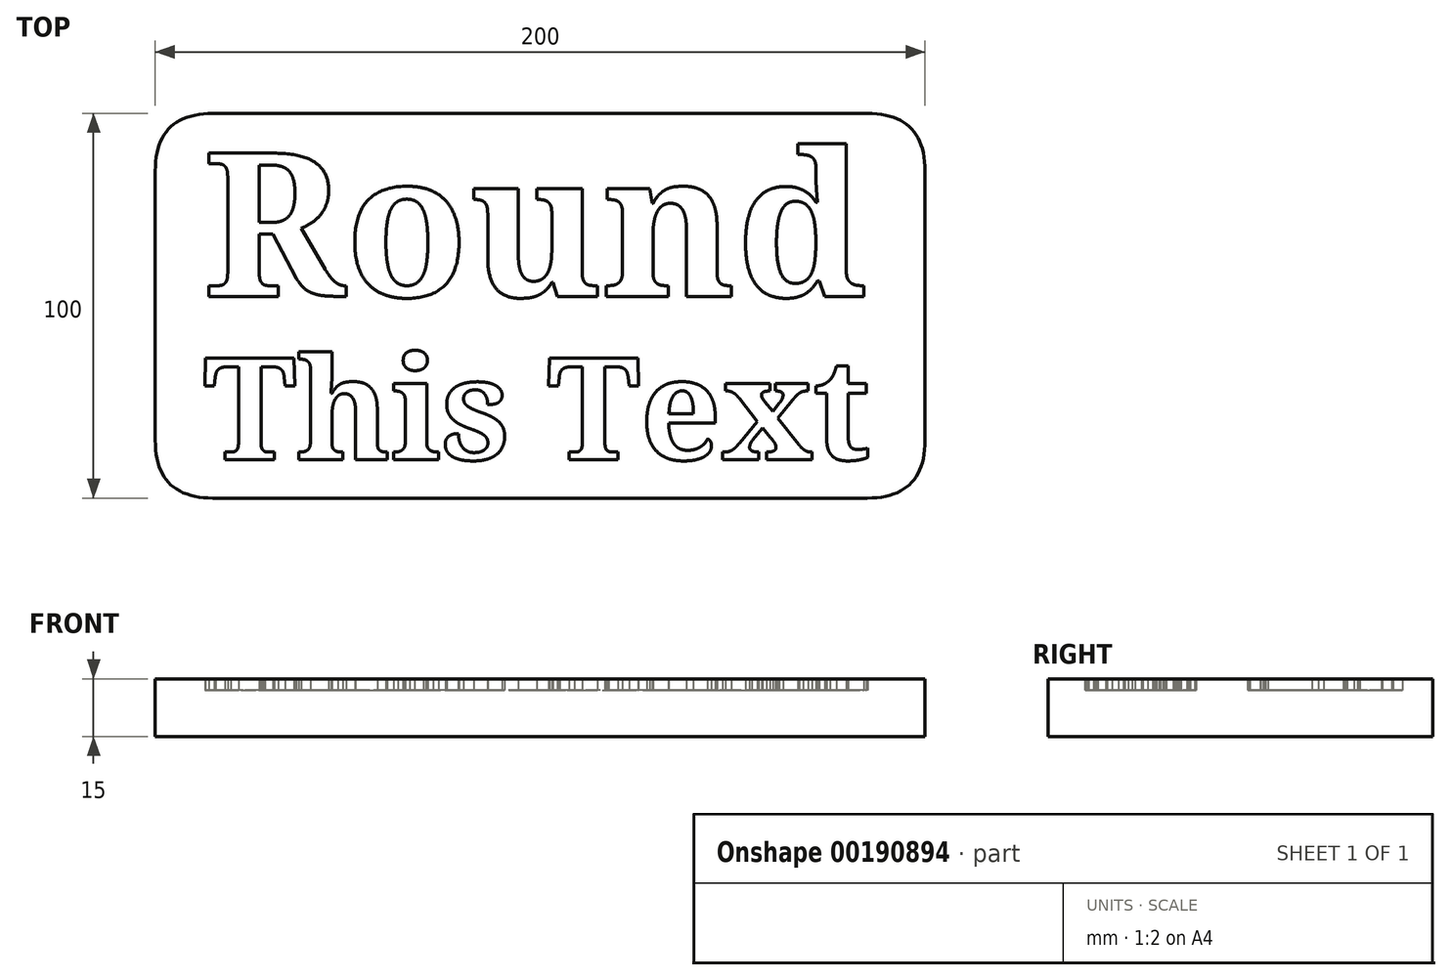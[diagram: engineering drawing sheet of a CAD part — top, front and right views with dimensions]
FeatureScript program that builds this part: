
annotation { "Feature Type Name" : "Feature", "Feature Type Description" : "" }
export const myFeature = defineFeature(function(context is Context, id is Id, definition is map)
    precondition{}
    {
        {
            var Q0;
            Q0=qCreatedBy(makeId("Top.planeOp"),FACE);
            var sketch = newSketch(context, id + "F0", { "sketchPlane" : qUnion([Q0])});
            skLineSegment(sketch, "E0.bottom", {"start": v(100, 50) * mm, "end": v(-100, 50) * mm});
            skLineSegment(sketch, "E0.top", {"start": v(100, -50) * mm, "end": v(-100, -50) * mm});
            skLineSegment(sketch, "E0.left", {"start": v(100, 50) * mm, "end": v(100, -50) * mm});
            skLineSegment(sketch, "E0.right", {"start": v(-100, 50) * mm, "end": v(-100, -50) * mm});
            skPoint(sketch, "E0.middle", {"position": v(0, 0) * mm});
            skText(sketch, "E1", { "text": "Round", "fontName": "NotoSerif-Bold.ttf"});
            skText(sketch, "E2", { "text": "This Text", "fontName": "NotoSerif-Bold.ttf"});
            skLineSegment(sketch, "E3", {"start": v(87.5, 40) * mm, "end": v(87.5, -40) * mm, "construction": true});
            const initialGuessF0  = {"E1": [-0.0875, 0.00243, 1, 0, 0.03757], "E2": [-0.0875, -0.04, 1, 0, 0.02659]};
            skSetInitialGuess(sketch, initialGuessF0);
            skSolve(sketch);
        }
        {
            var Q0;
            Q0 = qSketchRegion(id + "F0", true);
            var Q1;
            Q1=makeQuery(id+"F0.imprint","IMPRINT",FACE,{"disambiguationData":[TD([[makeQuery(id+"F0.imprint","IMPRINT",EDGE,{"derivedFrom":sQuery(id+"F0.wireOp",EDGE,"E1.sketch_text.stroke-42")}),1.0]])]});
            var Q2;
            Q2=makeQuery(id+"F0.imprint","IMPRINT",FACE,{"disambiguationData":[TD([[makeQuery(id+"F0.imprint","IMPRINT",EDGE,{"derivedFrom":sQuery(id+"F0.wireOp",EDGE,"E1.sketch_text.stroke-65")}),1.0]])]});
            var Q3;
            Q3=makeQuery(id+"F0.imprint","IMPRINT",FACE,{"disambiguationData":[TD([[makeQuery(id+"F0.imprint","IMPRINT",EDGE,{"derivedFrom":sQuery(id+"F0.wireOp",EDGE,"E1.sketch_text.stroke-211")}),1.0]])]});
            var Q4;
            Q4=makeQuery(id+"F0.imprint","IMPRINT",FACE,{"disambiguationData":[TD([[makeQuery(id+"F0.imprint","IMPRINT",EDGE,{"derivedFrom":sQuery(id+"F0.wireOp",EDGE,"E2.sketch_text.stroke-206")}),1.0]])]});
            extrude(context, id + "F1", {"entities" : qUnion([Q0, Q1, Q2, Q3, Q4]), "depth" : 15 * mm, "offsetDistance" : 25 * mm});
        }
        {
            var Q0;
            Q0=qCreatedBy(makeId("Top.planeOp"),FACE);
            var sketch = newSketch(context, id + "F2", { "sketchPlane" : qUnion([Q0])});
            skLineSegment(sketch, "E4.0", {"start": v(100, -50) * mm, "end": v(-100, -50) * mm});
            skLineSegment(sketch, "E4.1", {"start": v(-100, 50) * mm, "end": v(-100, -50) * mm});
            skLineSegment(sketch, "E4.2", {"start": v(100, 50) * mm, "end": v(100, -50) * mm});
            skLineSegment(sketch, "E4.3", {"start": v(100, 50) * mm, "end": v(-100, 50) * mm});
            skSolve(sketch);
        }
        {
            var Q0;
            Q0 = qSketchRegion(id + "F2", true);
            var Q1;
            Q1=makeQuery(id+"F1.opExtrude","CAP_FACE",FACE,{"disambiguationData":[OSD([sQuery(id+"F0.wireOp",EDGE,"E0.bottom"),sQuery(id+"F0.wireOp",EDGE,"E0.top"),sQuery(id+"F0.wireOp",EDGE,"E0.left"),sQuery(id+"F0.wireOp",EDGE,"E0.right"),sQuery(id+"F0.wireOp",EDGE,"E1.sketch_text.stroke-0"),sQuery(id+"F0.wireOp",EDGE,"E1.sketch_text.stroke-1"),sQuery(id+"F0.wireOp",EDGE,"E1.sketch_text.stroke-2"),sQuery(id+"F0.wireOp",EDGE,"E1.sketch_text.stroke-3"),sQuery(id+"F0.wireOp",EDGE,"E1.sketch_text.stroke-4"),sQuery(id+"F0.wireOp",EDGE,"E1.sketch_text.stroke-5"),sQuery(id+"F0.wireOp",EDGE,"E1.sketch_text.stroke-6"),sQuery(id+"F0.wireOp",EDGE,"E1.sketch_text.stroke-7"),sQuery(id+"F0.wireOp",EDGE,"E1.sketch_text.stroke-8"),sQuery(id+"F0.wireOp",EDGE,"E1.sketch_text.stroke-9"),sQuery(id+"F0.wireOp",EDGE,"E1.sketch_text.stroke-10"),sQuery(id+"F0.wireOp",EDGE,"E1.sketch_text.stroke-11"),sQuery(id+"F0.wireOp",EDGE,"E1.sketch_text.stroke-12"),sQuery(id+"F0.wireOp",EDGE,"E1.sketch_text.stroke-13"),sQuery(id+"F0.wireOp",EDGE,"E1.sketch_text.stroke-14"),sQuery(id+"F0.wireOp",EDGE,"E1.sketch_text.stroke-15"),sQuery(id+"F0.wireOp",EDGE,"E1.sketch_text.stroke-16"),sQuery(id+"F0.wireOp",EDGE,"E1.sketch_text.stroke-17"),sQuery(id+"F0.wireOp",EDGE,"E1.sketch_text.stroke-18"),sQuery(id+"F0.wireOp",EDGE,"E1.sketch_text.stroke-19"),sQuery(id+"F0.wireOp",EDGE,"E1.sketch_text.stroke-20"),sQuery(id+"F0.wireOp",EDGE,"E1.sketch_text.stroke-21"),sQuery(id+"F0.wireOp",EDGE,"E1.sketch_text.stroke-22"),sQuery(id+"F0.wireOp",EDGE,"E1.sketch_text.stroke-23"),sQuery(id+"F0.wireOp",EDGE,"E1.sketch_text.stroke-24"),sQuery(id+"F0.wireOp",EDGE,"E1.sketch_text.stroke-25"),sQuery(id+"F0.wireOp",EDGE,"E1.sketch_text.stroke-26"),sQuery(id+"F0.wireOp",EDGE,"E1.sketch_text.stroke-27"),sQuery(id+"F0.wireOp",EDGE,"E1.sketch_text.stroke-28"),sQuery(id+"F0.wireOp",EDGE,"E1.sketch_text.stroke-29"),sQuery(id+"F0.wireOp",EDGE,"E1.sketch_text.stroke-30"),sQuery(id+"F0.wireOp",EDGE,"E1.sketch_text.stroke-31"),sQuery(id+"F0.wireOp",EDGE,"E1.sketch_text.stroke-32"),sQuery(id+"F0.wireOp",EDGE,"E1.sketch_text.stroke-33"),sQuery(id+"F0.wireOp",EDGE,"E1.sketch_text.stroke-34"),sQuery(id+"F0.wireOp",EDGE,"E1.sketch_text.stroke-35"),sQuery(id+"F0.wireOp",EDGE,"E1.sketch_text.stroke-36"),sQuery(id+"F0.wireOp",EDGE,"E1.sketch_text.stroke-37"),sQuery(id+"F0.wireOp",EDGE,"E1.sketch_text.stroke-38"),sQuery(id+"F0.wireOp",EDGE,"E1.sketch_text.stroke-39"),sQuery(id+"F0.wireOp",EDGE,"E1.sketch_text.stroke-40"),sQuery(id+"F0.wireOp",EDGE,"E1.sketch_text.stroke-41"),sQuery(id+"F0.wireOp",EDGE,"E1.sketch_text.stroke-53"),sQuery(id+"F0.wireOp",EDGE,"E1.sketch_text.stroke-54"),sQuery(id+"F0.wireOp",EDGE,"E1.sketch_text.stroke-55"),sQuery(id+"F0.wireOp",EDGE,"E1.sketch_text.stroke-56"),sQuery(id+"F0.wireOp",EDGE,"E1.sketch_text.stroke-57"),sQuery(id+"F0.wireOp",EDGE,"E1.sketch_text.stroke-58"),sQuery(id+"F0.wireOp",EDGE,"E1.sketch_text.stroke-59"),sQuery(id+"F0.wireOp",EDGE,"E1.sketch_text.stroke-60"),sQuery(id+"F0.wireOp",EDGE,"E1.sketch_text.stroke-61"),sQuery(id+"F0.wireOp",EDGE,"E1.sketch_text.stroke-62"),sQuery(id+"F0.wireOp",EDGE,"E1.sketch_text.stroke-63"),sQuery(id+"F0.wireOp",EDGE,"E1.sketch_text.stroke-64"),sQuery(id+"F0.wireOp",EDGE,"E1.sketch_text.stroke-81"),sQuery(id+"F0.wireOp",EDGE,"E1.sketch_text.stroke-82"),sQuery(id+"F0.wireOp",EDGE,"E1.sketch_text.stroke-83"),sQuery(id+"F0.wireOp",EDGE,"E1.sketch_text.stroke-84"),sQuery(id+"F0.wireOp",EDGE,"E1.sketch_text.stroke-85"),sQuery(id+"F0.wireOp",EDGE,"E1.sketch_text.stroke-86"),sQuery(id+"F0.wireOp",EDGE,"E1.sketch_text.stroke-87"),sQuery(id+"F0.wireOp",EDGE,"E1.sketch_text.stroke-88"),sQuery(id+"F0.wireOp",EDGE,"E1.sketch_text.stroke-89"),sQuery(id+"F0.wireOp",EDGE,"E1.sketch_text.stroke-90"),sQuery(id+"F0.wireOp",EDGE,"E1.sketch_text.stroke-91"),sQuery(id+"F0.wireOp",EDGE,"E1.sketch_text.stroke-92"),sQuery(id+"F0.wireOp",EDGE,"E1.sketch_text.stroke-93"),sQuery(id+"F0.wireOp",EDGE,"E1.sketch_text.stroke-94"),sQuery(id+"F0.wireOp",EDGE,"E1.sketch_text.stroke-95"),sQuery(id+"F0.wireOp",EDGE,"E1.sketch_text.stroke-96"),sQuery(id+"F0.wireOp",EDGE,"E1.sketch_text.stroke-97"),sQuery(id+"F0.wireOp",EDGE,"E1.sketch_text.stroke-98"),sQuery(id+"F0.wireOp",EDGE,"E1.sketch_text.stroke-99"),sQuery(id+"F0.wireOp",EDGE,"E1.sketch_text.stroke-100"),sQuery(id+"F0.wireOp",EDGE,"E1.sketch_text.stroke-101"),sQuery(id+"F0.wireOp",EDGE,"E1.sketch_text.stroke-102"),sQuery(id+"F0.wireOp",EDGE,"E1.sketch_text.stroke-103"),sQuery(id+"F0.wireOp",EDGE,"E1.sketch_text.stroke-104"),sQuery(id+"F0.wireOp",EDGE,"E1.sketch_text.stroke-105"),sQuery(id+"F0.wireOp",EDGE,"E1.sketch_text.stroke-106"),sQuery(id+"F0.wireOp",EDGE,"E1.sketch_text.stroke-107"),sQuery(id+"F0.wireOp",EDGE,"E1.sketch_text.stroke-108"),sQuery(id+"F0.wireOp",EDGE,"E1.sketch_text.stroke-109"),sQuery(id+"F0.wireOp",EDGE,"E1.sketch_text.stroke-110"),sQuery(id+"F0.wireOp",EDGE,"E1.sketch_text.stroke-111"),sQuery(id+"F0.wireOp",EDGE,"E1.sketch_text.stroke-112"),sQuery(id+"F0.wireOp",EDGE,"E1.sketch_text.stroke-113"),sQuery(id+"F0.wireOp",EDGE,"E1.sketch_text.stroke-114"),sQuery(id+"F0.wireOp",EDGE,"E1.sketch_text.stroke-115"),sQuery(id+"F0.wireOp",EDGE,"E1.sketch_text.stroke-116"),sQuery(id+"F0.wireOp",EDGE,"E1.sketch_text.stroke-117"),sQuery(id+"F0.wireOp",EDGE,"E1.sketch_text.stroke-118"),sQuery(id+"F0.wireOp",EDGE,"E1.sketch_text.stroke-119"),sQuery(id+"F0.wireOp",EDGE,"E1.sketch_text.stroke-120"),sQuery(id+"F0.wireOp",EDGE,"E1.sketch_text.stroke-121"),sQuery(id+"F0.wireOp",EDGE,"E1.sketch_text.stroke-122"),sQuery(id+"F0.wireOp",EDGE,"E1.sketch_text.stroke-123"),sQuery(id+"F0.wireOp",EDGE,"E1.sketch_text.stroke-124"),sQuery(id+"F0.wireOp",EDGE,"E1.sketch_text.stroke-125"),sQuery(id+"F0.wireOp",EDGE,"E1.sketch_text.stroke-126"),sQuery(id+"F0.wireOp",EDGE,"E1.sketch_text.stroke-127"),sQuery(id+"F0.wireOp",EDGE,"E1.sketch_text.stroke-128"),sQuery(id+"F0.wireOp",EDGE,"E1.sketch_text.stroke-129"),sQuery(id+"F0.wireOp",EDGE,"E1.sketch_text.stroke-130"),sQuery(id+"F0.wireOp",EDGE,"E1.sketch_text.stroke-131"),sQuery(id+"F0.wireOp",EDGE,"E1.sketch_text.stroke-132"),sQuery(id+"F0.wireOp",EDGE,"E1.sketch_text.stroke-133"),sQuery(id+"F0.wireOp",EDGE,"E1.sketch_text.stroke-134"),sQuery(id+"F0.wireOp",EDGE,"E1.sketch_text.stroke-135"),sQuery(id+"F0.wireOp",EDGE,"E1.sketch_text.stroke-136"),sQuery(id+"F0.wireOp",EDGE,"E1.sketch_text.stroke-137"),sQuery(id+"F0.wireOp",EDGE,"E1.sketch_text.stroke-138"),sQuery(id+"F0.wireOp",EDGE,"E1.sketch_text.stroke-139"),sQuery(id+"F0.wireOp",EDGE,"E1.sketch_text.stroke-140"),sQuery(id+"F0.wireOp",EDGE,"E1.sketch_text.stroke-141"),sQuery(id+"F0.wireOp",EDGE,"E1.sketch_text.stroke-142"),sQuery(id+"F0.wireOp",EDGE,"E1.sketch_text.stroke-143"),sQuery(id+"F0.wireOp",EDGE,"E1.sketch_text.stroke-144"),sQuery(id+"F0.wireOp",EDGE,"E1.sketch_text.stroke-145"),sQuery(id+"F0.wireOp",EDGE,"E1.sketch_text.stroke-146"),sQuery(id+"F0.wireOp",EDGE,"E1.sketch_text.stroke-147"),sQuery(id+"F0.wireOp",EDGE,"E1.sketch_text.stroke-148"),sQuery(id+"F0.wireOp",EDGE,"E1.sketch_text.stroke-149"),sQuery(id+"F0.wireOp",EDGE,"E1.sketch_text.stroke-150"),sQuery(id+"F0.wireOp",EDGE,"E1.sketch_text.stroke-151"),sQuery(id+"F0.wireOp",EDGE,"E1.sketch_text.stroke-152"),sQuery(id+"F0.wireOp",EDGE,"E1.sketch_text.stroke-153"),sQuery(id+"F0.wireOp",EDGE,"E1.sketch_text.stroke-154"),sQuery(id+"F0.wireOp",EDGE,"E1.sketch_text.stroke-155"),sQuery(id+"F0.wireOp",EDGE,"E1.sketch_text.stroke-156"),sQuery(id+"F0.wireOp",EDGE,"E1.sketch_text.stroke-157"),sQuery(id+"F0.wireOp",EDGE,"E1.sketch_text.stroke-158"),sQuery(id+"F0.wireOp",EDGE,"E1.sketch_text.stroke-159"),sQuery(id+"F0.wireOp",EDGE,"E1.sketch_text.stroke-160"),sQuery(id+"F0.wireOp",EDGE,"E1.sketch_text.stroke-161"),sQuery(id+"F0.wireOp",EDGE,"E1.sketch_text.stroke-162"),sQuery(id+"F0.wireOp",EDGE,"E1.sketch_text.stroke-163"),sQuery(id+"F0.wireOp",EDGE,"E1.sketch_text.stroke-164"),sQuery(id+"F0.wireOp",EDGE,"E1.sketch_text.stroke-165"),sQuery(id+"F0.wireOp",EDGE,"E1.sketch_text.stroke-166"),sQuery(id+"F0.wireOp",EDGE,"E1.sketch_text.stroke-167"),sQuery(id+"F0.wireOp",EDGE,"E1.sketch_text.stroke-168"),sQuery(id+"F0.wireOp",EDGE,"E1.sketch_text.stroke-169"),sQuery(id+"F0.wireOp",EDGE,"E1.sketch_text.stroke-170"),sQuery(id+"F0.wireOp",EDGE,"E1.sketch_text.stroke-171"),sQuery(id+"F0.wireOp",EDGE,"E1.sketch_text.stroke-172"),sQuery(id+"F0.wireOp",EDGE,"E1.sketch_text.stroke-173"),sQuery(id+"F0.wireOp",EDGE,"E1.sketch_text.stroke-174"),sQuery(id+"F0.wireOp",EDGE,"E1.sketch_text.stroke-175"),sQuery(id+"F0.wireOp",EDGE,"E1.sketch_text.stroke-176"),sQuery(id+"F0.wireOp",EDGE,"E1.sketch_text.stroke-177"),sQuery(id+"F0.wireOp",EDGE,"E1.sketch_text.stroke-178"),sQuery(id+"F0.wireOp",EDGE,"E1.sketch_text.stroke-179"),sQuery(id+"F0.wireOp",EDGE,"E1.sketch_text.stroke-180"),sQuery(id+"F0.wireOp",EDGE,"E1.sketch_text.stroke-181"),sQuery(id+"F0.wireOp",EDGE,"E1.sketch_text.stroke-182"),sQuery(id+"F0.wireOp",EDGE,"E1.sketch_text.stroke-183"),sQuery(id+"F0.wireOp",EDGE,"E1.sketch_text.stroke-184"),sQuery(id+"F0.wireOp",EDGE,"E1.sketch_text.stroke-185"),sQuery(id+"F0.wireOp",EDGE,"E1.sketch_text.stroke-186"),sQuery(id+"F0.wireOp",EDGE,"E1.sketch_text.stroke-187"),sQuery(id+"F0.wireOp",EDGE,"E1.sketch_text.stroke-188"),sQuery(id+"F0.wireOp",EDGE,"E1.sketch_text.stroke-189"),sQuery(id+"F0.wireOp",EDGE,"E1.sketch_text.stroke-190"),sQuery(id+"F0.wireOp",EDGE,"E1.sketch_text.stroke-191"),sQuery(id+"F0.wireOp",EDGE,"E1.sketch_text.stroke-192"),sQuery(id+"F0.wireOp",EDGE,"E1.sketch_text.stroke-193"),sQuery(id+"F0.wireOp",EDGE,"E1.sketch_text.stroke-194"),sQuery(id+"F0.wireOp",EDGE,"E1.sketch_text.stroke-195"),sQuery(id+"F0.wireOp",EDGE,"E1.sketch_text.stroke-196"),sQuery(id+"F0.wireOp",EDGE,"E1.sketch_text.stroke-197"),sQuery(id+"F0.wireOp",EDGE,"E1.sketch_text.stroke-198"),sQuery(id+"F0.wireOp",EDGE,"E1.sketch_text.stroke-199"),sQuery(id+"F0.wireOp",EDGE,"E1.sketch_text.stroke-200"),sQuery(id+"F0.wireOp",EDGE,"E1.sketch_text.stroke-201"),sQuery(id+"F0.wireOp",EDGE,"E1.sketch_text.stroke-202"),sQuery(id+"F0.wireOp",EDGE,"E1.sketch_text.stroke-203"),sQuery(id+"F0.wireOp",EDGE,"E1.sketch_text.stroke-204"),sQuery(id+"F0.wireOp",EDGE,"E1.sketch_text.stroke-205"),sQuery(id+"F0.wireOp",EDGE,"E1.sketch_text.stroke-206"),sQuery(id+"F0.wireOp",EDGE,"E1.sketch_text.stroke-207"),sQuery(id+"F0.wireOp",EDGE,"E1.sketch_text.stroke-208"),sQuery(id+"F0.wireOp",EDGE,"E1.sketch_text.stroke-209"),sQuery(id+"F0.wireOp",EDGE,"E1.sketch_text.stroke-210"),sQuery(id+"F0.wireOp",EDGE,"E2.sketch_text.stroke-0"),sQuery(id+"F0.wireOp",EDGE,"E2.sketch_text.stroke-1"),sQuery(id+"F0.wireOp",EDGE,"E2.sketch_text.stroke-2"),sQuery(id+"F0.wireOp",EDGE,"E2.sketch_text.stroke-3"),sQuery(id+"F0.wireOp",EDGE,"E2.sketch_text.stroke-4"),sQuery(id+"F0.wireOp",EDGE,"E2.sketch_text.stroke-5"),sQuery(id+"F0.wireOp",EDGE,"E2.sketch_text.stroke-6"),sQuery(id+"F0.wireOp",EDGE,"E2.sketch_text.stroke-7"),sQuery(id+"F0.wireOp",EDGE,"E2.sketch_text.stroke-8"),sQuery(id+"F0.wireOp",EDGE,"E2.sketch_text.stroke-9"),sQuery(id+"F0.wireOp",EDGE,"E2.sketch_text.stroke-10"),sQuery(id+"F0.wireOp",EDGE,"E2.sketch_text.stroke-11"),sQuery(id+"F0.wireOp",EDGE,"E2.sketch_text.stroke-12"),sQuery(id+"F0.wireOp",EDGE,"E2.sketch_text.stroke-13"),sQuery(id+"F0.wireOp",EDGE,"E2.sketch_text.stroke-14"),sQuery(id+"F0.wireOp",EDGE,"E2.sketch_text.stroke-15"),sQuery(id+"F0.wireOp",EDGE,"E2.sketch_text.stroke-16"),sQuery(id+"F0.wireOp",EDGE,"E2.sketch_text.stroke-17"),sQuery(id+"F0.wireOp",EDGE,"E2.sketch_text.stroke-18"),sQuery(id+"F0.wireOp",EDGE,"E2.sketch_text.stroke-19"),sQuery(id+"F0.wireOp",EDGE,"E2.sketch_text.stroke-20"),sQuery(id+"F0.wireOp",EDGE,"E2.sketch_text.stroke-21"),sQuery(id+"F0.wireOp",EDGE,"E2.sketch_text.stroke-22"),sQuery(id+"F0.wireOp",EDGE,"E2.sketch_text.stroke-23"),sQuery(id+"F0.wireOp",EDGE,"E2.sketch_text.stroke-24"),sQuery(id+"F0.wireOp",EDGE,"E2.sketch_text.stroke-25"),sQuery(id+"F0.wireOp",EDGE,"E2.sketch_text.stroke-26"),sQuery(id+"F0.wireOp",EDGE,"E2.sketch_text.stroke-27"),sQuery(id+"F0.wireOp",EDGE,"E2.sketch_text.stroke-28"),sQuery(id+"F0.wireOp",EDGE,"E2.sketch_text.stroke-29"),sQuery(id+"F0.wireOp",EDGE,"E2.sketch_text.stroke-30"),sQuery(id+"F0.wireOp",EDGE,"E2.sketch_text.stroke-31"),sQuery(id+"F0.wireOp",EDGE,"E2.sketch_text.stroke-32"),sQuery(id+"F0.wireOp",EDGE,"E2.sketch_text.stroke-33"),sQuery(id+"F0.wireOp",EDGE,"E2.sketch_text.stroke-34"),sQuery(id+"F0.wireOp",EDGE,"E2.sketch_text.stroke-35"),sQuery(id+"F0.wireOp",EDGE,"E2.sketch_text.stroke-36"),sQuery(id+"F0.wireOp",EDGE,"E2.sketch_text.stroke-37"),sQuery(id+"F0.wireOp",EDGE,"E2.sketch_text.stroke-38"),sQuery(id+"F0.wireOp",EDGE,"E2.sketch_text.stroke-39"),sQuery(id+"F0.wireOp",EDGE,"E2.sketch_text.stroke-40"),sQuery(id+"F0.wireOp",EDGE,"E2.sketch_text.stroke-41"),sQuery(id+"F0.wireOp",EDGE,"E2.sketch_text.stroke-42"),sQuery(id+"F0.wireOp",EDGE,"E2.sketch_text.stroke-43"),sQuery(id+"F0.wireOp",EDGE,"E2.sketch_text.stroke-44"),sQuery(id+"F0.wireOp",EDGE,"E2.sketch_text.stroke-45"),sQuery(id+"F0.wireOp",EDGE,"E2.sketch_text.stroke-46"),sQuery(id+"F0.wireOp",EDGE,"E2.sketch_text.stroke-47"),sQuery(id+"F0.wireOp",EDGE,"E2.sketch_text.stroke-48"),sQuery(id+"F0.wireOp",EDGE,"E2.sketch_text.stroke-49"),sQuery(id+"F0.wireOp",EDGE,"E2.sketch_text.stroke-50"),sQuery(id+"F0.wireOp",EDGE,"E2.sketch_text.stroke-51"),sQuery(id+"F0.wireOp",EDGE,"E2.sketch_text.stroke-52"),sQuery(id+"F0.wireOp",EDGE,"E2.sketch_text.stroke-53"),sQuery(id+"F0.wireOp",EDGE,"E2.sketch_text.stroke-54"),sQuery(id+"F0.wireOp",EDGE,"E2.sketch_text.stroke-55"),sQuery(id+"F0.wireOp",EDGE,"E2.sketch_text.stroke-56"),sQuery(id+"F0.wireOp",EDGE,"E2.sketch_text.stroke-57"),sQuery(id+"F0.wireOp",EDGE,"E2.sketch_text.stroke-58"),sQuery(id+"F0.wireOp",EDGE,"E2.sketch_text.stroke-59"),sQuery(id+"F0.wireOp",EDGE,"E2.sketch_text.stroke-60"),sQuery(id+"F0.wireOp",EDGE,"E2.sketch_text.stroke-61"),sQuery(id+"F0.wireOp",EDGE,"E2.sketch_text.stroke-62"),sQuery(id+"F0.wireOp",EDGE,"E2.sketch_text.stroke-63"),sQuery(id+"F0.wireOp",EDGE,"E2.sketch_text.stroke-64"),sQuery(id+"F0.wireOp",EDGE,"E2.sketch_text.stroke-65"),sQuery(id+"F0.wireOp",EDGE,"E2.sketch_text.stroke-66"),sQuery(id+"F0.wireOp",EDGE,"E2.sketch_text.stroke-67"),sQuery(id+"F0.wireOp",EDGE,"E2.sketch_text.stroke-68"),sQuery(id+"F0.wireOp",EDGE,"E2.sketch_text.stroke-69"),sQuery(id+"F0.wireOp",EDGE,"E2.sketch_text.stroke-70"),sQuery(id+"F0.wireOp",EDGE,"E2.sketch_text.stroke-71"),sQuery(id+"F0.wireOp",EDGE,"E2.sketch_text.stroke-72"),sQuery(id+"F0.wireOp",EDGE,"E2.sketch_text.stroke-73"),sQuery(id+"F0.wireOp",EDGE,"E2.sketch_text.stroke-74"),sQuery(id+"F0.wireOp",EDGE,"E2.sketch_text.stroke-75"),sQuery(id+"F0.wireOp",EDGE,"E2.sketch_text.stroke-76"),sQuery(id+"F0.wireOp",EDGE,"E2.sketch_text.stroke-77"),sQuery(id+"F0.wireOp",EDGE,"E2.sketch_text.stroke-78"),sQuery(id+"F0.wireOp",EDGE,"E2.sketch_text.stroke-79"),sQuery(id+"F0.wireOp",EDGE,"E2.sketch_text.stroke-80"),sQuery(id+"F0.wireOp",EDGE,"E2.sketch_text.stroke-81"),sQuery(id+"F0.wireOp",EDGE,"E2.sketch_text.stroke-82"),sQuery(id+"F0.wireOp",EDGE,"E2.sketch_text.stroke-83"),sQuery(id+"F0.wireOp",EDGE,"E2.sketch_text.stroke-84"),sQuery(id+"F0.wireOp",EDGE,"E2.sketch_text.stroke-85"),sQuery(id+"F0.wireOp",EDGE,"E2.sketch_text.stroke-86"),sQuery(id+"F0.wireOp",EDGE,"E2.sketch_text.stroke-87"),sQuery(id+"F0.wireOp",EDGE,"E2.sketch_text.stroke-88"),sQuery(id+"F0.wireOp",EDGE,"E2.sketch_text.stroke-89"),sQuery(id+"F0.wireOp",EDGE,"E2.sketch_text.stroke-90"),sQuery(id+"F0.wireOp",EDGE,"E2.sketch_text.stroke-91"),sQuery(id+"F0.wireOp",EDGE,"E2.sketch_text.stroke-92"),sQuery(id+"F0.wireOp",EDGE,"E2.sketch_text.stroke-93"),sQuery(id+"F0.wireOp",EDGE,"E2.sketch_text.stroke-94"),sQuery(id+"F0.wireOp",EDGE,"E2.sketch_text.stroke-95"),sQuery(id+"F0.wireOp",EDGE,"E2.sketch_text.stroke-96"),sQuery(id+"F0.wireOp",EDGE,"E2.sketch_text.stroke-97"),sQuery(id+"F0.wireOp",EDGE,"E2.sketch_text.stroke-98"),sQuery(id+"F0.wireOp",EDGE,"E2.sketch_text.stroke-99"),sQuery(id+"F0.wireOp",EDGE,"E2.sketch_text.stroke-100"),sQuery(id+"F0.wireOp",EDGE,"E2.sketch_text.stroke-101"),sQuery(id+"F0.wireOp",EDGE,"E2.sketch_text.stroke-102"),sQuery(id+"F0.wireOp",EDGE,"E2.sketch_text.stroke-103"),sQuery(id+"F0.wireOp",EDGE,"E2.sketch_text.stroke-104"),sQuery(id+"F0.wireOp",EDGE,"E2.sketch_text.stroke-105"),sQuery(id+"F0.wireOp",EDGE,"E2.sketch_text.stroke-106"),sQuery(id+"F0.wireOp",EDGE,"E2.sketch_text.stroke-107"),sQuery(id+"F0.wireOp",EDGE,"E2.sketch_text.stroke-108"),sQuery(id+"F0.wireOp",EDGE,"E2.sketch_text.stroke-109"),sQuery(id+"F0.wireOp",EDGE,"E2.sketch_text.stroke-110"),sQuery(id+"F0.wireOp",EDGE,"E2.sketch_text.stroke-111"),sQuery(id+"F0.wireOp",EDGE,"E2.sketch_text.stroke-112"),sQuery(id+"F0.wireOp",EDGE,"E2.sketch_text.stroke-113"),sQuery(id+"F0.wireOp",EDGE,"E2.sketch_text.stroke-114"),sQuery(id+"F0.wireOp",EDGE,"E2.sketch_text.stroke-115"),sQuery(id+"F0.wireOp",EDGE,"E2.sketch_text.stroke-116"),sQuery(id+"F0.wireOp",EDGE,"E2.sketch_text.stroke-117"),sQuery(id+"F0.wireOp",EDGE,"E2.sketch_text.stroke-118"),sQuery(id+"F0.wireOp",EDGE,"E2.sketch_text.stroke-119"),sQuery(id+"F0.wireOp",EDGE,"E2.sketch_text.stroke-120"),sQuery(id+"F0.wireOp",EDGE,"E2.sketch_text.stroke-121"),sQuery(id+"F0.wireOp",EDGE,"E2.sketch_text.stroke-122"),sQuery(id+"F0.wireOp",EDGE,"E2.sketch_text.stroke-123"),sQuery(id+"F0.wireOp",EDGE,"E2.sketch_text.stroke-124"),sQuery(id+"F0.wireOp",EDGE,"E2.sketch_text.stroke-125"),sQuery(id+"F0.wireOp",EDGE,"E2.sketch_text.stroke-126"),sQuery(id+"F0.wireOp",EDGE,"E2.sketch_text.stroke-127"),sQuery(id+"F0.wireOp",EDGE,"E2.sketch_text.stroke-128"),sQuery(id+"F0.wireOp",EDGE,"E2.sketch_text.stroke-129"),sQuery(id+"F0.wireOp",EDGE,"E2.sketch_text.stroke-130"),sQuery(id+"F0.wireOp",EDGE,"E2.sketch_text.stroke-131"),sQuery(id+"F0.wireOp",EDGE,"E2.sketch_text.stroke-132"),sQuery(id+"F0.wireOp",EDGE,"E2.sketch_text.stroke-133"),sQuery(id+"F0.wireOp",EDGE,"E2.sketch_text.stroke-134"),sQuery(id+"F0.wireOp",EDGE,"E2.sketch_text.stroke-135"),sQuery(id+"F0.wireOp",EDGE,"E2.sketch_text.stroke-136"),sQuery(id+"F0.wireOp",EDGE,"E2.sketch_text.stroke-137"),sQuery(id+"F0.wireOp",EDGE,"E2.sketch_text.stroke-138"),sQuery(id+"F0.wireOp",EDGE,"E2.sketch_text.stroke-139"),sQuery(id+"F0.wireOp",EDGE,"E2.sketch_text.stroke-140"),sQuery(id+"F0.wireOp",EDGE,"E2.sketch_text.stroke-141"),sQuery(id+"F0.wireOp",EDGE,"E2.sketch_text.stroke-142"),sQuery(id+"F0.wireOp",EDGE,"E2.sketch_text.stroke-143"),sQuery(id+"F0.wireOp",EDGE,"E2.sketch_text.stroke-144"),sQuery(id+"F0.wireOp",EDGE,"E2.sketch_text.stroke-145"),sQuery(id+"F0.wireOp",EDGE,"E2.sketch_text.stroke-146"),sQuery(id+"F0.wireOp",EDGE,"E2.sketch_text.stroke-147"),sQuery(id+"F0.wireOp",EDGE,"E2.sketch_text.stroke-148"),sQuery(id+"F0.wireOp",EDGE,"E2.sketch_text.stroke-149"),sQuery(id+"F0.wireOp",EDGE,"E2.sketch_text.stroke-150"),sQuery(id+"F0.wireOp",EDGE,"E2.sketch_text.stroke-151"),sQuery(id+"F0.wireOp",EDGE,"E2.sketch_text.stroke-152"),sQuery(id+"F0.wireOp",EDGE,"E2.sketch_text.stroke-153"),sQuery(id+"F0.wireOp",EDGE,"E2.sketch_text.stroke-154"),sQuery(id+"F0.wireOp",EDGE,"E2.sketch_text.stroke-155"),sQuery(id+"F0.wireOp",EDGE,"E2.sketch_text.stroke-156"),sQuery(id+"F0.wireOp",EDGE,"E2.sketch_text.stroke-157"),sQuery(id+"F0.wireOp",EDGE,"E2.sketch_text.stroke-158"),sQuery(id+"F0.wireOp",EDGE,"E2.sketch_text.stroke-159"),sQuery(id+"F0.wireOp",EDGE,"E2.sketch_text.stroke-160"),sQuery(id+"F0.wireOp",EDGE,"E2.sketch_text.stroke-161"),sQuery(id+"F0.wireOp",EDGE,"E2.sketch_text.stroke-162"),sQuery(id+"F0.wireOp",EDGE,"E2.sketch_text.stroke-163"),sQuery(id+"F0.wireOp",EDGE,"E2.sketch_text.stroke-164"),sQuery(id+"F0.wireOp",EDGE,"E2.sketch_text.stroke-165"),sQuery(id+"F0.wireOp",EDGE,"E2.sketch_text.stroke-166"),sQuery(id+"F0.wireOp",EDGE,"E2.sketch_text.stroke-167"),sQuery(id+"F0.wireOp",EDGE,"E2.sketch_text.stroke-168"),sQuery(id+"F0.wireOp",EDGE,"E2.sketch_text.stroke-169"),sQuery(id+"F0.wireOp",EDGE,"E2.sketch_text.stroke-170"),sQuery(id+"F0.wireOp",EDGE,"E2.sketch_text.stroke-171"),sQuery(id+"F0.wireOp",EDGE,"E2.sketch_text.stroke-172"),sQuery(id+"F0.wireOp",EDGE,"E2.sketch_text.stroke-173"),sQuery(id+"F0.wireOp",EDGE,"E2.sketch_text.stroke-174"),sQuery(id+"F0.wireOp",EDGE,"E2.sketch_text.stroke-175"),sQuery(id+"F0.wireOp",EDGE,"E2.sketch_text.stroke-176"),sQuery(id+"F0.wireOp",EDGE,"E2.sketch_text.stroke-177"),sQuery(id+"F0.wireOp",EDGE,"E2.sketch_text.stroke-178"),sQuery(id+"F0.wireOp",EDGE,"E2.sketch_text.stroke-179"),sQuery(id+"F0.wireOp",EDGE,"E2.sketch_text.stroke-180"),sQuery(id+"F0.wireOp",EDGE,"E2.sketch_text.stroke-181"),sQuery(id+"F0.wireOp",EDGE,"E2.sketch_text.stroke-182"),sQuery(id+"F0.wireOp",EDGE,"E2.sketch_text.stroke-183"),sQuery(id+"F0.wireOp",EDGE,"E2.sketch_text.stroke-184"),sQuery(id+"F0.wireOp",EDGE,"E2.sketch_text.stroke-185"),sQuery(id+"F0.wireOp",EDGE,"E2.sketch_text.stroke-186"),sQuery(id+"F0.wireOp",EDGE,"E2.sketch_text.stroke-187"),sQuery(id+"F0.wireOp",EDGE,"E2.sketch_text.stroke-188"),sQuery(id+"F0.wireOp",EDGE,"E2.sketch_text.stroke-189"),sQuery(id+"F0.wireOp",EDGE,"E2.sketch_text.stroke-190"),sQuery(id+"F0.wireOp",EDGE,"E2.sketch_text.stroke-191"),sQuery(id+"F0.wireOp",EDGE,"E2.sketch_text.stroke-192"),sQuery(id+"F0.wireOp",EDGE,"E2.sketch_text.stroke-193"),sQuery(id+"F0.wireOp",EDGE,"E2.sketch_text.stroke-194"),sQuery(id+"F0.wireOp",EDGE,"E2.sketch_text.stroke-195"),sQuery(id+"F0.wireOp",EDGE,"E2.sketch_text.stroke-196"),sQuery(id+"F0.wireOp",EDGE,"E2.sketch_text.stroke-197"),sQuery(id+"F0.wireOp",EDGE,"E2.sketch_text.stroke-198"),sQuery(id+"F0.wireOp",EDGE,"E2.sketch_text.stroke-199"),sQuery(id+"F0.wireOp",EDGE,"E2.sketch_text.stroke-200"),sQuery(id+"F0.wireOp",EDGE,"E2.sketch_text.stroke-201"),sQuery(id+"F0.wireOp",EDGE,"E2.sketch_text.stroke-202"),sQuery(id+"F0.wireOp",EDGE,"E2.sketch_text.stroke-203"),sQuery(id+"F0.wireOp",EDGE,"E2.sketch_text.stroke-204"),sQuery(id+"F0.wireOp",EDGE,"E2.sketch_text.stroke-205"),sQuery(id+"F0.wireOp",EDGE,"E2.sketch_text.stroke-213"),sQuery(id+"F0.wireOp",EDGE,"E2.sketch_text.stroke-214"),sQuery(id+"F0.wireOp",EDGE,"E2.sketch_text.stroke-215"),sQuery(id+"F0.wireOp",EDGE,"E2.sketch_text.stroke-216"),sQuery(id+"F0.wireOp",EDGE,"E2.sketch_text.stroke-217"),sQuery(id+"F0.wireOp",EDGE,"E2.sketch_text.stroke-218"),sQuery(id+"F0.wireOp",EDGE,"E2.sketch_text.stroke-219"),sQuery(id+"F0.wireOp",EDGE,"E2.sketch_text.stroke-220"),sQuery(id+"F0.wireOp",EDGE,"E2.sketch_text.stroke-221"),sQuery(id+"F0.wireOp",EDGE,"E2.sketch_text.stroke-222"),sQuery(id+"F0.wireOp",EDGE,"E2.sketch_text.stroke-223"),sQuery(id+"F0.wireOp",EDGE,"E2.sketch_text.stroke-224"),sQuery(id+"F0.wireOp",EDGE,"E2.sketch_text.stroke-225"),sQuery(id+"F0.wireOp",EDGE,"E2.sketch_text.stroke-226"),sQuery(id+"F0.wireOp",EDGE,"E2.sketch_text.stroke-227"),sQuery(id+"F0.wireOp",EDGE,"E2.sketch_text.stroke-228"),sQuery(id+"F0.wireOp",EDGE,"E2.sketch_text.stroke-229"),sQuery(id+"F0.wireOp",EDGE,"E2.sketch_text.stroke-230"),sQuery(id+"F0.wireOp",EDGE,"E2.sketch_text.stroke-231"),sQuery(id+"F0.wireOp",EDGE,"E2.sketch_text.stroke-232"),sQuery(id+"F0.wireOp",EDGE,"E2.sketch_text.stroke-233"),sQuery(id+"F0.wireOp",EDGE,"E2.sketch_text.stroke-234"),sQuery(id+"F0.wireOp",EDGE,"E2.sketch_text.stroke-235"),sQuery(id+"F0.wireOp",EDGE,"E2.sketch_text.stroke-236"),sQuery(id+"F0.wireOp",EDGE,"E2.sketch_text.stroke-237"),sQuery(id+"F0.wireOp",EDGE,"E2.sketch_text.stroke-238"),sQuery(id+"F0.wireOp",EDGE,"E2.sketch_text.stroke-239"),sQuery(id+"F0.wireOp",EDGE,"E2.sketch_text.stroke-240"),sQuery(id+"F0.wireOp",EDGE,"E2.sketch_text.stroke-241"),sQuery(id+"F0.wireOp",EDGE,"E2.sketch_text.stroke-242"),sQuery(id+"F0.wireOp",EDGE,"E2.sketch_text.stroke-243"),sQuery(id+"F0.wireOp",EDGE,"E2.sketch_text.stroke-244"),sQuery(id+"F0.wireOp",EDGE,"E2.sketch_text.stroke-245"),sQuery(id+"F0.wireOp",EDGE,"E2.sketch_text.stroke-246"),sQuery(id+"F0.wireOp",EDGE,"E2.sketch_text.stroke-247"),sQuery(id+"F0.wireOp",EDGE,"E2.sketch_text.stroke-248"),sQuery(id+"F0.wireOp",EDGE,"E2.sketch_text.stroke-249"),sQuery(id+"F0.wireOp",EDGE,"E2.sketch_text.stroke-250"),sQuery(id+"F0.wireOp",EDGE,"E2.sketch_text.stroke-251"),sQuery(id+"F0.wireOp",EDGE,"E2.sketch_text.stroke-252"),sQuery(id+"F0.wireOp",EDGE,"E2.sketch_text.stroke-253"),sQuery(id+"F0.wireOp",EDGE,"E2.sketch_text.stroke-254"),sQuery(id+"F0.wireOp",EDGE,"E2.sketch_text.stroke-255"),sQuery(id+"F0.wireOp",EDGE,"E2.sketch_text.stroke-256"),sQuery(id+"F0.wireOp",EDGE,"E2.sketch_text.stroke-257"),sQuery(id+"F0.wireOp",EDGE,"E2.sketch_text.stroke-258"),sQuery(id+"F0.wireOp",EDGE,"E2.sketch_text.stroke-259"),sQuery(id+"F0.wireOp",EDGE,"E2.sketch_text.stroke-260"),sQuery(id+"F0.wireOp",EDGE,"E2.sketch_text.stroke-261"),sQuery(id+"F0.wireOp",EDGE,"E2.sketch_text.stroke-262"),sQuery(id+"F0.wireOp",EDGE,"E2.sketch_text.stroke-263"),sQuery(id+"F0.wireOp",EDGE,"E2.sketch_text.stroke-264"),sQuery(id+"F0.wireOp",EDGE,"E2.sketch_text.stroke-265"),sQuery(id+"F0.wireOp",EDGE,"E2.sketch_text.stroke-266"),sQuery(id+"F0.wireOp",EDGE,"E2.sketch_text.stroke-267"),sQuery(id+"F0.wireOp",EDGE,"E2.sketch_text.stroke-268"),sQuery(id+"F0.wireOp",EDGE,"E2.sketch_text.stroke-269"),sQuery(id+"F0.wireOp",EDGE,"E2.sketch_text.stroke-270"),sQuery(id+"F0.wireOp",EDGE,"E2.sketch_text.stroke-271"),sQuery(id+"F0.wireOp",EDGE,"E2.sketch_text.stroke-272"),sQuery(id+"F0.wireOp",EDGE,"E2.sketch_text.stroke-273"),sQuery(id+"F0.wireOp",EDGE,"E2.sketch_text.stroke-274"),sQuery(id+"F0.wireOp",EDGE,"E2.sketch_text.stroke-275"),sQuery(id+"F0.wireOp",EDGE,"E2.sketch_text.stroke-276"),sQuery(id+"F0.wireOp",EDGE,"E2.sketch_text.stroke-277"),sQuery(id+"F0.wireOp",EDGE,"E2.sketch_text.stroke-278"),sQuery(id+"F0.wireOp",EDGE,"E2.sketch_text.stroke-279"),sQuery(id+"F0.wireOp",EDGE,"E2.sketch_text.stroke-280"),sQuery(id+"F0.wireOp",EDGE,"E2.sketch_text.stroke-281"),sQuery(id+"F0.wireOp",EDGE,"E2.sketch_text.stroke-282"),sQuery(id+"F0.wireOp",EDGE,"E2.sketch_text.stroke-283"),sQuery(id+"F0.wireOp",EDGE,"E2.sketch_text.stroke-284"),sQuery(id+"F0.wireOp",EDGE,"E2.sketch_text.stroke-285"),sQuery(id+"F0.wireOp",EDGE,"E2.sketch_text.stroke-286"),sQuery(id+"F0.wireOp",EDGE,"E2.sketch_text.stroke-287"),sQuery(id+"F0.wireOp",EDGE,"E2.sketch_text.stroke-288"),sQuery(id+"F0.wireOp",EDGE,"E2.sketch_text.stroke-289"),sQuery(id+"F0.wireOp",EDGE,"E2.sketch_text.stroke-290"),sQuery(id+"F0.wireOp",EDGE,"E2.sketch_text.stroke-291"),sQuery(id+"F0.wireOp",EDGE,"E2.sketch_text.stroke-292"),sQuery(id+"F0.wireOp",EDGE,"E2.sketch_text.stroke-293"),sQuery(id+"F0.wireOp",EDGE,"E2.sketch_text.stroke-294"),sQuery(id+"F0.wireOp",EDGE,"E2.sketch_text.stroke-295"),sQuery(id+"F0.wireOp",EDGE,"E2.sketch_text.stroke-296"),sQuery(id+"F0.wireOp",EDGE,"E2.sketch_text.stroke-297"),sQuery(id+"F0.wireOp",EDGE,"E2.sketch_text.stroke-298"),sQuery(id+"F0.wireOp",EDGE,"E2.sketch_text.stroke-299"),sQuery(id+"F0.wireOp",EDGE,"E2.sketch_text.stroke-300"),sQuery(id+"F0.wireOp",EDGE,"E2.sketch_text.stroke-301"),sQuery(id+"F0.wireOp",EDGE,"E2.sketch_text.stroke-302"),sQuery(id+"F0.wireOp",EDGE,"E2.sketch_text.stroke-303"),sQuery(id+"F0.wireOp",EDGE,"E2.sketch_text.stroke-304"),sQuery(id+"F0.wireOp",EDGE,"E2.sketch_text.stroke-305"),sQuery(id+"F0.wireOp",EDGE,"E2.sketch_text.stroke-306"),sQuery(id+"F0.wireOp",EDGE,"E2.sketch_text.stroke-307"),sQuery(id+"F0.wireOp",EDGE,"E2.sketch_text.stroke-308"),sQuery(id+"F0.wireOp",EDGE,"E2.sketch_text.stroke-309"),sQuery(id+"F0.wireOp",EDGE,"E2.sketch_text.stroke-310"),sQuery(id+"F0.wireOp",EDGE,"E2.sketch_text.stroke-311"),sQuery(id+"F0.wireOp",EDGE,"E2.sketch_text.stroke-312"),sQuery(id+"F0.wireOp",EDGE,"E2.sketch_text.stroke-313"),sQuery(id+"F0.wireOp",EDGE,"E2.sketch_text.stroke-314"),sQuery(id+"F0.wireOp",EDGE,"E2.sketch_text.stroke-315"),sQuery(id+"F0.wireOp",EDGE,"E2.sketch_text.stroke-316"),sQuery(id+"F0.wireOp",EDGE,"E2.sketch_text.stroke-317"),sQuery(id+"F0.wireOp",EDGE,"E2.sketch_text.stroke-318"),sQuery(id+"F0.wireOp",EDGE,"E2.sketch_text.stroke-319"),sQuery(id+"F0.wireOp",EDGE,"E2.sketch_text.stroke-320"),sQuery(id+"F0.wireOp",EDGE,"E2.sketch_text.stroke-321"),sQuery(id+"F0.wireOp",EDGE,"E2.sketch_text.stroke-322"),sQuery(id+"F0.wireOp",EDGE,"E2.sketch_text.stroke-323")])],"isStart":false});
            extrude(context, id + "F3", {"entities" : qUnion([Q0]), "operationType" : NewBodyOperationType.ADD, "endBound" : BoundingType.UP_TO_SURFACE, "depth" : 25 * mm, "endBoundEntityFace" : qUnion([Q1]), "hasOffset" : true, "offsetDistance" : 3 * mm});
        }
        {
            var Q0;
            Q0=makeQuery(id+"F1.opExtrude","SWEPT_EDGE",EDGE,{"disambiguationData":[OSD([sQuery(id+"F0.wireOp",EDGE,"E0.top"),sQuery(id+"F0.wireOp",EDGE,"E0.right")])]});
            var Q1;
            Q1=makeQuery(id+"F1.opExtrude","SWEPT_EDGE",EDGE,{"disambiguationData":[OSD([sQuery(id+"F0.wireOp",EDGE,"E0.top"),sQuery(id+"F0.wireOp",EDGE,"E0.left")])]});
            var Q2;
            Q2=makeQuery(id+"F1.opExtrude","SWEPT_EDGE",EDGE,{"disambiguationData":[OSD([sQuery(id+"F0.wireOp",EDGE,"E0.bottom"),sQuery(id+"F0.wireOp",EDGE,"E0.left")])]});
            var Q3;
            Q3=makeQuery(id+"F1.opExtrude","SWEPT_EDGE",EDGE,{"disambiguationData":[OSD([sQuery(id+"F0.wireOp",EDGE,"E0.bottom"),sQuery(id+"F0.wireOp",EDGE,"E0.right")])]});
            fillet(context, id + "F4", {"entities" : qUnion([Q0, Q1, Q2, Q3]), "radius" : 15 * mm, "tangentPropagation" : true, "rho" : 0.5, "crossSection" : FilletCrossSection.CONIC, "allowEdgeOverflow" : false});
        }
    });
